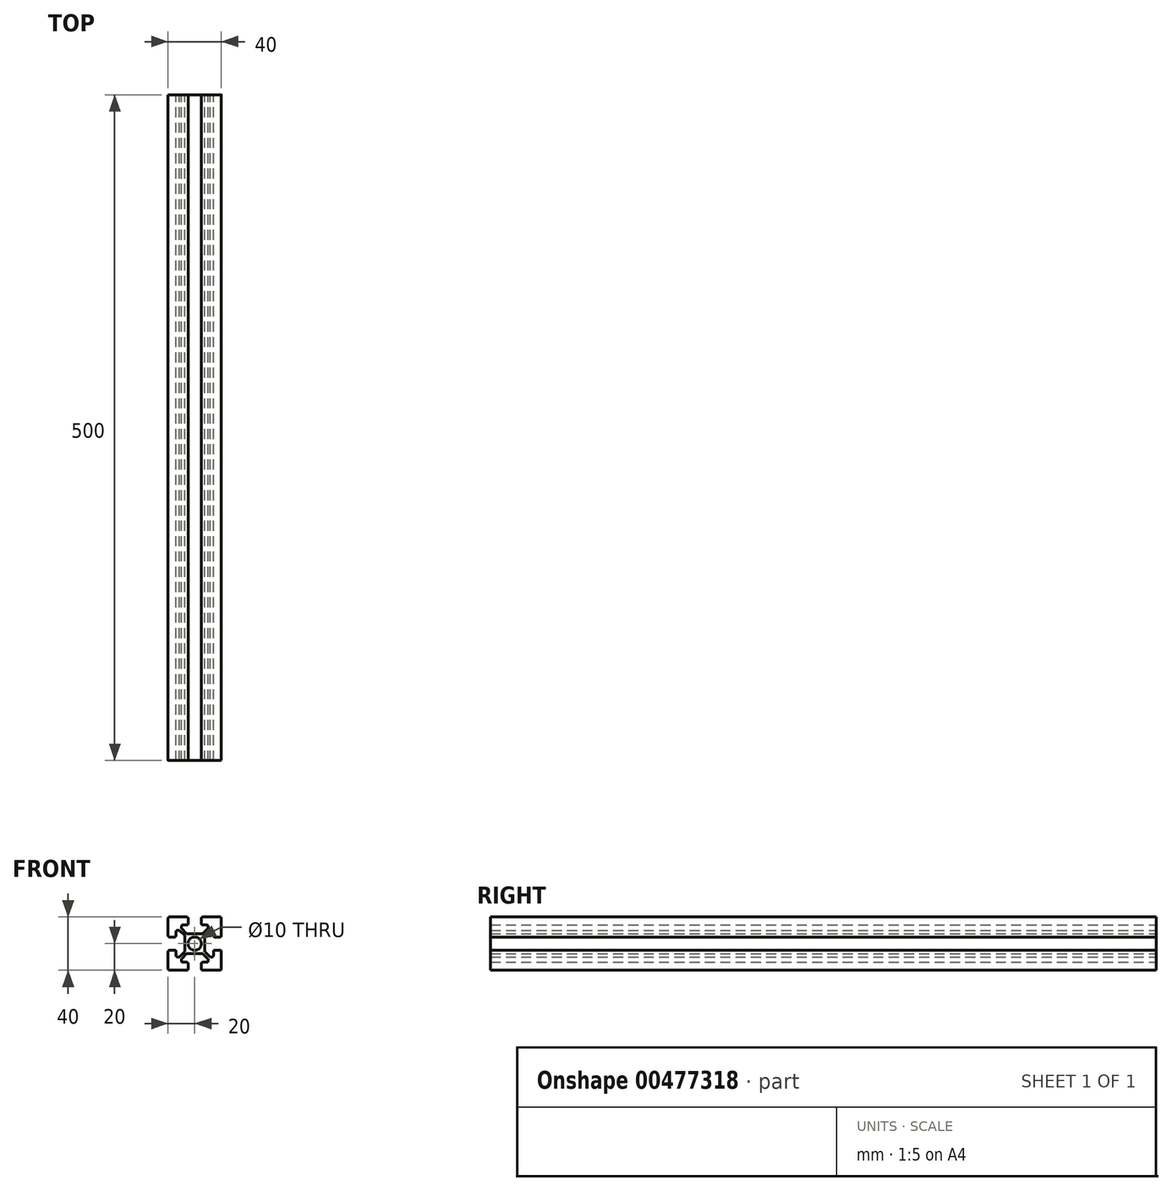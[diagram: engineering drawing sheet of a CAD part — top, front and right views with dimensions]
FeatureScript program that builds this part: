
annotation { "Feature Type Name" : "Feature", "Feature Type Description" : "" }
export const myFeature = defineFeature(function(context is Context, id is Id, definition is map)
    precondition{}
    {
        {
            var Q0;
            Q0=qCreatedBy(makeId("Front.planeOp"),FACE);
            var sketch = newSketch(context, id + "F0", { "sketchPlane" : qUnion([Q0])});
            skLineSegment(sketch, "E0.bottom", {"start": v(20, 20) * mm, "end": v(-20, 20) * mm});
            skLineSegment(sketch, "E0.top", {"start": v(20, -20) * mm, "end": v(-20, -20) * mm});
            skLineSegment(sketch, "E0.left", {"start": v(20, 20) * mm, "end": v(20, -20) * mm});
            skLineSegment(sketch, "E0.right", {"start": v(-20, 20) * mm, "end": v(-20, -20) * mm});
            skPoint(sketch, "E0.middle", {"position": v(0, 0) * mm});
            skLineSegment(sketch, "E1.bottom", {"start": v(14, 5) * mm, "end": v(20, 5) * mm});
            skLineSegment(sketch, "E1.top", {"start": v(14, -5) * mm, "end": v(20, -5) * mm});
            skPoint(sketch, "E1.middle", {"position": v(20, 0) * mm});
            skLineSegment(sketch, "E2.bottom", {"start": v(14, 10.05) * mm, "end": v(11.5, 10.05) * mm});
            skLineSegment(sketch, "E2.top", {"start": v(14, -10.05) * mm, "end": v(11.5, -10.05) * mm});
            skLineSegment(sketch, "E2.left", {"start": v(14, 10.05) * mm, "end": v(14, 5) * mm});
            skLineSegment(sketch, "E2.right", {"start": v(7.5, 6.05) * mm, "end": v(7.5, -6.05) * mm});
            skPoint(sketch, "E2.middle", {"position": v(10.75, 0) * mm});
            skLineSegment(sketch, "E3.trimOffspring", {"start": v(14, -5) * mm, "end": v(14, -10.05) * mm});
            skLineSegment(sketch, "E4", {"start": v(7.5, 6.05) * mm, "end": v(11.5, 10.05) * mm});
            skLineSegment(sketch, "E5.MirrorCS", {"start": v(7.5, -6.05) * mm, "end": v(11.5, -10.05) * mm});
            skLineSegment(sketch, "E6.1.0", {"start": v(5, 14) * mm, "end": v(5, 20) * mm});
            skLineSegment(sketch, "E6.1.1", {"start": v(-5, 14) * mm, "end": v(-5, 20) * mm});
            skLineSegment(sketch, "E6.1.2", {"start": v(-6.05, 7.5) * mm, "end": v(6.05, 7.5) * mm});
            skLineSegment(sketch, "E6.1.3", {"start": v(5, 14) * mm, "end": v(10.05, 14) * mm});
            skLineSegment(sketch, "E6.1.4", {"start": v(-6.05, 7.5) * mm, "end": v(-10.05, 11.5) * mm});
            skPoint(sketch, "E6.1.5", {"position": v(0, 10.75) * mm});
            skLineSegment(sketch, "E6.1.6", {"start": v(6.05, 7.5) * mm, "end": v(10.05, 11.5) * mm});
            skPoint(sketch, "E6.1.7", {"position": v(0, 20) * mm});
            skLineSegment(sketch, "E6.1.8", {"start": v(-10.05, 14) * mm, "end": v(-5, 14) * mm});
            skLineSegment(sketch, "E6.1.9", {"start": v(-10.05, 14) * mm, "end": v(-10.05, 11.5) * mm});
            skLineSegment(sketch, "E6.1.10", {"start": v(10.05, 14) * mm, "end": v(10.05, 11.5) * mm});
            skLineSegment(sketch, "E6.2.0", {"start": v(-14, 5) * mm, "end": v(-20, 5) * mm});
            skLineSegment(sketch, "E6.2.1", {"start": v(-14, -5) * mm, "end": v(-20, -5) * mm});
            skLineSegment(sketch, "E6.2.2", {"start": v(-7.5, -6.05) * mm, "end": v(-7.5, 6.05) * mm});
            skLineSegment(sketch, "E6.2.3", {"start": v(-14, 5) * mm, "end": v(-14, 10.05) * mm});
            skLineSegment(sketch, "E6.2.4", {"start": v(-7.5, -6.05) * mm, "end": v(-11.5, -10.05) * mm});
            skPoint(sketch, "E6.2.5", {"position": v(-10.75, 0) * mm});
            skLineSegment(sketch, "E6.2.6", {"start": v(-7.5, 6.05) * mm, "end": v(-11.5, 10.05) * mm});
            skPoint(sketch, "E6.2.7", {"position": v(-20, 0) * mm});
            skLineSegment(sketch, "E6.2.8", {"start": v(-14, -10.05) * mm, "end": v(-14, -5) * mm});
            skLineSegment(sketch, "E6.2.9", {"start": v(-14, -10.05) * mm, "end": v(-11.5, -10.05) * mm});
            skLineSegment(sketch, "E6.2.10", {"start": v(-14, 10.05) * mm, "end": v(-11.5, 10.05) * mm});
            skLineSegment(sketch, "E6.3.0", {"start": v(-5, -14) * mm, "end": v(-5, -20) * mm});
            skLineSegment(sketch, "E6.3.1", {"start": v(5, -14) * mm, "end": v(5, -20) * mm});
            skLineSegment(sketch, "E6.3.2", {"start": v(6.05, -7.5) * mm, "end": v(-6.05, -7.5) * mm});
            skLineSegment(sketch, "E6.3.3", {"start": v(-5, -14) * mm, "end": v(-10.05, -14) * mm});
            skLineSegment(sketch, "E6.3.4", {"start": v(6.05, -7.5) * mm, "end": v(10.05, -11.5) * mm});
            skPoint(sketch, "E6.3.5", {"position": v(0, -10.75) * mm});
            skLineSegment(sketch, "E6.3.6", {"start": v(-6.05, -7.5) * mm, "end": v(-10.05, -11.5) * mm});
            skPoint(sketch, "E6.3.7", {"position": v(0, -20) * mm});
            skLineSegment(sketch, "E6.3.8", {"start": v(10.05, -14) * mm, "end": v(5, -14) * mm});
            skLineSegment(sketch, "E6.3.9", {"start": v(10.05, -14) * mm, "end": v(10.05, -11.5) * mm});
            skLineSegment(sketch, "E6.3.10", {"start": v(-10.05, -14) * mm, "end": v(-10.05, -11.5) * mm});
            skCircle(sketch, "E7", {"center": v(0, 0) * mm, "radius": 5 * mm});
            skSolve(sketch);
        }
        {
            var Q0;
            {var subQ14=sQuery(id+"F0.wireOp",EDGE,"E1.bottom");Q0=makeQuery(id+"F0.imprint","IMPRINT",FACE,{"disambiguationData":[TD([[makeQuery(id+"F0.imprint","IMPRINT",EDGE,{"derivedFrom":subQ14}),1.0]])]});}
            extrude(context, id + "F1", {"entities" : qUnion([Q0]), "endBound" : BoundingType.SYMMETRIC, "depth" : 500 * mm});
        }
        {
            var Q0;
            Q0=makeQuery(id+"F1.opExtrude","SWEPT_EDGE",EDGE,{"disambiguationData":[OSD([sQuery(id+"F0.wireOp",EDGE,"E0.bottom"),sQuery(id+"F0.wireOp",EDGE,"E6.1.1")])]});
            var Q1;
            Q1=makeQuery(id+"F1.opExtrude","SWEPT_EDGE",EDGE,{"disambiguationData":[OSD([sQuery(id+"F0.wireOp",EDGE,"E0.bottom"),sQuery(id+"F0.wireOp",EDGE,"E6.1.0")])]});
            var Q2;
            Q2=makeQuery(id+"F1.opExtrude","SWEPT_EDGE",EDGE,{"disambiguationData":[OSD([sQuery(id+"F0.wireOp",EDGE,"E0.bottom"),sQuery(id+"F0.wireOp",EDGE,"E0.left")])]});
            var Q3;
            Q3=makeQuery(id+"F1.opExtrude","SWEPT_EDGE",EDGE,{"disambiguationData":[OSD([sQuery(id+"F0.wireOp",EDGE,"E0.left"),sQuery(id+"F0.wireOp",EDGE,"E1.bottom")])]});
            var Q4;
            Q4=makeQuery(id+"F1.opExtrude","SWEPT_EDGE",EDGE,{"disambiguationData":[OSD([sQuery(id+"F0.wireOp",EDGE,"E6.1.1"),sQuery(id+"F0.wireOp",EDGE,"E6.1.8")])]});
            var Q5;
            Q5=makeQuery(id+"F1.opExtrude","SWEPT_EDGE",EDGE,{"disambiguationData":[OSD([sQuery(id+"F0.wireOp",EDGE,"E6.1.2"),sQuery(id+"F0.wireOp",EDGE,"E6.1.4")])]});
            var Q6;
            Q6=makeQuery(id+"F1.opExtrude","SWEPT_EDGE",EDGE,{"disambiguationData":[OSD([sQuery(id+"F0.wireOp",EDGE,"E6.1.4"),sQuery(id+"F0.wireOp",EDGE,"E6.1.9")])]});
            var Q7;
            Q7=makeQuery(id+"F1.opExtrude","SWEPT_EDGE",EDGE,{"disambiguationData":[OSD([sQuery(id+"F0.wireOp",EDGE,"E6.1.8"),sQuery(id+"F0.wireOp",EDGE,"E6.1.9")])]});
            var Q8;
            Q8=makeQuery(id+"F1.opExtrude","SWEPT_EDGE",EDGE,{"disambiguationData":[OSD([sQuery(id+"F0.wireOp",EDGE,"E6.1.3"),sQuery(id+"F0.wireOp",EDGE,"E6.1.10")])]});
            var Q9;
            Q9=makeQuery(id+"F1.opExtrude","SWEPT_EDGE",EDGE,{"disambiguationData":[OSD([sQuery(id+"F0.wireOp",EDGE,"E6.1.0"),sQuery(id+"F0.wireOp",EDGE,"E6.1.3")])]});
            var Q10;
            Q10=makeQuery(id+"F1.opExtrude","SWEPT_EDGE",EDGE,{"disambiguationData":[OSD([sQuery(id+"F0.wireOp",EDGE,"E6.1.6"),sQuery(id+"F0.wireOp",EDGE,"E6.1.10")])]});
            var Q11;
            Q11=makeQuery(id+"F1.opExtrude","SWEPT_EDGE",EDGE,{"disambiguationData":[OSD([sQuery(id+"F0.wireOp",EDGE,"E6.1.2"),sQuery(id+"F0.wireOp",EDGE,"E6.1.6")])]});
            var Q12;
            Q12=makeQuery(id+"F1.opExtrude","SWEPT_EDGE",EDGE,{"disambiguationData":[OSD([sQuery(id+"F0.wireOp",EDGE,"E0.left"),sQuery(id+"F0.wireOp",EDGE,"E1.top")])]});
            var Q13;
            Q13=makeQuery(id+"F1.opExtrude","SWEPT_EDGE",EDGE,{"disambiguationData":[OSD([sQuery(id+"F0.wireOp",EDGE,"E1.top"),sQuery(id+"F0.wireOp",EDGE,"E3.trimOffspring")])]});
            var Q14;
            Q14=makeQuery(id+"F1.opExtrude","SWEPT_EDGE",EDGE,{"disambiguationData":[OSD([sQuery(id+"F0.wireOp",EDGE,"E2.right"),sQuery(id+"F0.wireOp",EDGE,"E4")])]});
            var Q15;
            Q15=makeQuery(id+"F1.opExtrude","SWEPT_EDGE",EDGE,{"disambiguationData":[OSD([sQuery(id+"F0.wireOp",EDGE,"E2.right"),sQuery(id+"F0.wireOp",EDGE,"E5.MirrorCS")])]});
            var Q16;
            Q16=makeQuery(id+"F1.opExtrude","SWEPT_EDGE",EDGE,{"disambiguationData":[OSD([sQuery(id+"F0.wireOp",EDGE,"E6.3.6"),sQuery(id+"F0.wireOp",EDGE,"E6.3.10")])]});
            var Q17;
            Q17=makeQuery(id+"F1.opExtrude","SWEPT_EDGE",EDGE,{"disambiguationData":[OSD([sQuery(id+"F0.wireOp",EDGE,"E6.3.3"),sQuery(id+"F0.wireOp",EDGE,"E6.3.10")])]});
            var Q18;
            Q18=makeQuery(id+"F1.opExtrude","SWEPT_EDGE",EDGE,{"disambiguationData":[OSD([sQuery(id+"F0.wireOp",EDGE,"E6.3.1"),sQuery(id+"F0.wireOp",EDGE,"E6.3.8")])]});
            var Q19;
            Q19=makeQuery(id+"F1.opExtrude","SWEPT_EDGE",EDGE,{"disambiguationData":[OSD([sQuery(id+"F0.wireOp",EDGE,"E0.top"),sQuery(id+"F0.wireOp",EDGE,"E0.left")])]});
            var Q20;
            Q20=makeQuery(id+"F1.opExtrude","SWEPT_EDGE",EDGE,{"disambiguationData":[OSD([sQuery(id+"F0.wireOp",EDGE,"E0.top"),sQuery(id+"F0.wireOp",EDGE,"E6.3.0")])]});
            var Q21;
            Q21=makeQuery(id+"F1.opExtrude","SWEPT_EDGE",EDGE,{"disambiguationData":[OSD([sQuery(id+"F0.wireOp",EDGE,"E6.2.1"),sQuery(id+"F0.wireOp",EDGE,"E6.2.8")])]});
            var Q22;
            Q22=makeQuery(id+"F1.opExtrude","SWEPT_EDGE",EDGE,{"disambiguationData":[OSD([sQuery(id+"F0.wireOp",EDGE,"E6.2.8"),sQuery(id+"F0.wireOp",EDGE,"E6.2.9")])]});
            var Q23;
            Q23=makeQuery(id+"F1.opExtrude","SWEPT_EDGE",EDGE,{"disambiguationData":[OSD([sQuery(id+"F0.wireOp",EDGE,"E6.2.0"),sQuery(id+"F0.wireOp",EDGE,"E6.2.3")])]});
            var Q24;
            Q24=makeQuery(id+"F1.opExtrude","SWEPT_EDGE",EDGE,{"disambiguationData":[OSD([sQuery(id+"F0.wireOp",EDGE,"E0.bottom"),sQuery(id+"F0.wireOp",EDGE,"E0.right")])]});
            var Q25;
            Q25=makeQuery(id+"F1.opExtrude","SWEPT_EDGE",EDGE,{"disambiguationData":[OSD([sQuery(id+"F0.wireOp",EDGE,"E2.top"),sQuery(id+"F0.wireOp",EDGE,"E3.trimOffspring")])]});
            var Q26;
            Q26=makeQuery(id+"F1.opExtrude","SWEPT_EDGE",EDGE,{"disambiguationData":[OSD([sQuery(id+"F0.wireOp",EDGE,"E6.3.4"),sQuery(id+"F0.wireOp",EDGE,"E6.3.9")])]});
            var Q27;
            Q27=makeQuery(id+"F1.opExtrude","SWEPT_EDGE",EDGE,{"disambiguationData":[OSD([sQuery(id+"F0.wireOp",EDGE,"E6.3.8"),sQuery(id+"F0.wireOp",EDGE,"E6.3.9")])]});
            var Q28;
            Q28=makeQuery(id+"F1.opExtrude","SWEPT_EDGE",EDGE,{"disambiguationData":[OSD([sQuery(id+"F0.wireOp",EDGE,"E6.3.0"),sQuery(id+"F0.wireOp",EDGE,"E6.3.3")])]});
            var Q29;
            Q29=makeQuery(id+"F1.opExtrude","SWEPT_EDGE",EDGE,{"disambiguationData":[OSD([sQuery(id+"F0.wireOp",EDGE,"E0.top"),sQuery(id+"F0.wireOp",EDGE,"E6.3.1")])]});
            var Q30;
            Q30=makeQuery(id+"F1.opExtrude","SWEPT_EDGE",EDGE,{"disambiguationData":[OSD([sQuery(id+"F0.wireOp",EDGE,"E6.2.3"),sQuery(id+"F0.wireOp",EDGE,"E6.2.10")])]});
            var Q31;
            Q31=makeQuery(id+"F1.opExtrude","SWEPT_EDGE",EDGE,{"disambiguationData":[OSD([sQuery(id+"F0.wireOp",EDGE,"E0.right"),sQuery(id+"F0.wireOp",EDGE,"E6.2.0")])]});
            var Q32;
            Q32=makeQuery(id+"F1.opExtrude","SWEPT_EDGE",EDGE,{"disambiguationData":[OSD([sQuery(id+"F0.wireOp",EDGE,"E0.right"),sQuery(id+"F0.wireOp",EDGE,"E6.2.1")])]});
            var Q33;
            Q33=makeQuery(id+"F1.opExtrude","SWEPT_EDGE",EDGE,{"disambiguationData":[OSD([sQuery(id+"F0.wireOp",EDGE,"E6.2.2"),sQuery(id+"F0.wireOp",EDGE,"E6.2.6")])]});
            var Q34;
            Q34=makeQuery(id+"F1.opExtrude","SWEPT_EDGE",EDGE,{"disambiguationData":[OSD([sQuery(id+"F0.wireOp",EDGE,"E6.2.2"),sQuery(id+"F0.wireOp",EDGE,"E6.2.4")])]});
            var Q35;
            Q35=makeQuery(id+"F1.opExtrude","SWEPT_EDGE",EDGE,{"disambiguationData":[OSD([sQuery(id+"F0.wireOp",EDGE,"E6.2.4"),sQuery(id+"F0.wireOp",EDGE,"E6.2.9")])]});
            var Q36;
            Q36=makeQuery(id+"F1.opExtrude","SWEPT_EDGE",EDGE,{"disambiguationData":[OSD([sQuery(id+"F0.wireOp",EDGE,"E2.bottom"),sQuery(id+"F0.wireOp",EDGE,"E2.left")])]});
            var Q37;
            Q37=makeQuery(id+"F1.opExtrude","SWEPT_EDGE",EDGE,{"disambiguationData":[OSD([sQuery(id+"F0.wireOp",EDGE,"E2.bottom"),sQuery(id+"F0.wireOp",EDGE,"E4")])]});
            var Q38;
            Q38=makeQuery(id+"F1.opExtrude","SWEPT_EDGE",EDGE,{"disambiguationData":[OSD([sQuery(id+"F0.wireOp",EDGE,"E1.bottom"),sQuery(id+"F0.wireOp",EDGE,"E2.left")])]});
            var Q39;
            Q39=makeQuery(id+"F1.opExtrude","SWEPT_EDGE",EDGE,{"disambiguationData":[OSD([sQuery(id+"F0.wireOp",EDGE,"E6.3.2"),sQuery(id+"F0.wireOp",EDGE,"E6.3.6")])]});
            var Q40;
            Q40=makeQuery(id+"F1.opExtrude","SWEPT_EDGE",EDGE,{"disambiguationData":[OSD([sQuery(id+"F0.wireOp",EDGE,"E6.3.2"),sQuery(id+"F0.wireOp",EDGE,"E6.3.4")])]});
            var Q41;
            Q41=makeQuery(id+"F1.opExtrude","SWEPT_EDGE",EDGE,{"disambiguationData":[OSD([sQuery(id+"F0.wireOp",EDGE,"E0.top"),sQuery(id+"F0.wireOp",EDGE,"E0.right")])]});
            fillet(context, id + "F2", {"entities" : qUnion([Q0, Q1, Q2, Q3, Q4, Q5, Q6, Q7, Q8, Q9, Q10, Q11, Q12, Q13, Q14, Q15, Q16, Q17, Q18, Q19, Q20, Q21, Q22, Q23, Q24, Q25, Q26, Q27, Q28, Q29, Q30, Q31, Q32, Q33, Q34, Q35, Q36, Q37, Q38, Q39, Q40, Q41]), "radius" : 1 * mm, "tangentPropagation" : true, "allowEdgeOverflow" : false});
        }
    });
